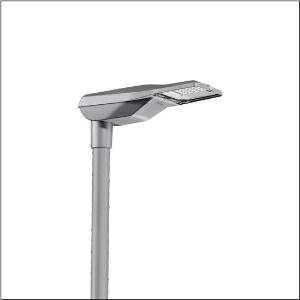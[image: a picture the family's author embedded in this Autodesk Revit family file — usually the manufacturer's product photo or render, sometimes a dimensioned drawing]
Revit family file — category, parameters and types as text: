
# Revit family: streetlight_sl_21_iq_micro___st1_0ab_5xe1m31g08cb_01f6
name_source: partatom
category: Lighting Fixtures
units: mm (PartAtom-declared; Revit-internal decimal feet)

## family parameters
Cut with Voids When Loaded = No
Host = Face
Light Source = No
Part Type = Normal
Room Calculation Point = No
Round Connector Dimension = Use Diameter
Shared = No

## types (1)
- --- (1 x LED, 2520 lm, 19.4 W, 3000K)
    Apparent Load = 19 VA
    CIE Flux Codes = 38 73 97 100 100
    Color Rendering = 70
    Color Temperature = 3000K
    Default Elevation = 1800 mm
    Description = Streetlight SL 21 iQ micro, mast luminaire, primary light control with lens, of PMMA, primary optical cover: cover, of toughened safety glass, transparent, light distribution: ST1.0aB, light emission: direct distribution, primary light characteristic: asymmetric, installation type: post-top, side-entry, LED, High Power LED, rated luminous flux: 2.520lm, luminous efficacy: 130lm/W, light colour: 730, colour temperature: 3000K, control: Street-Remote, Auto-Match, Temp-Guard, Lumen-Switch, Night-Set, Smart-Wire, Light-Fading, Desk-Remote (wireless, voltage-free reading and setting of iQ features in the workshop via application-optimized NFC function/RFID function), optimised constant luminous flux control (CLO 2.0), pre-setting: linear dimming characteristic, mains connection: 220..240V, AC, 50/60Hz, start of lifetime: 19W, end of service life: 20W, reduction: 10W, luminaire housing, of diecast aluminium, powder-coated, Siteco® metallic grey (DB 702S), corrosivity category C5 mid according to DIN EN ISO 12944, please order mast flange separately, inclination adjustable: 0°, 5°, 10°, 15°, sealing non-destructively replaceable, multi-level sealing system, length: 528mm, width: 235mm, height: 110mm, mast flange for spigot size: 42mm (side-entry): 5XC10008XM4, 60/48mm (side-entry/post-top): 5XC10108XM2, 76/60mm (side-entry/post-top): 5XC10108XM1, protection rating (complete): IP66, insulation class (complete): insulation class II (safety insulation), certification: CE, ENEC, ENEC+, VDE, impact resistance: IK09, permissible operating ambient temperature for outdoor applications: -40..+50°C, standard-compliant lighting for roads and squares, packaging unit: 1 piece

Light Distribution: ST1.0aB
    Height = 110 mm
    Lamp = 1 x LED
    Lamp Light Flux = 2520 lm
    Lamp Power = 19.4 W
    Lamp count = 1
    Length = 528 mm
    Luminous efficacy = 130 lm/W
    Manufacturer = Siteco
    ModVariant = No
    Model = 5XE1M31G08CB
    Number of Poles = 1
    OnlyDefault = Yes
    Power Factor = 1
    Product Name = Streetlight SL 21 iQ micro | ST1.0aB
    Product group = mast luminaire | pylon top
    ProductGroupID = 6100
    Protection Class = Protection class II
    Protection Degree = IP 66
    RLX_Detail_Level = 1
    RLX_Emergency_Light_Flux = 0 lm
    RLX_Emergency_Type = 0
    RLX_Emergency_Type_DB = No
    RlxData = <blob elided: 99149 chars, md5=1984a4cd>
    Socket = socket
    Standby Power = 0 W
    System Light Flux = 2520 lm
    System Power = 19 W
    Type Comments = factory setting: luminous flux: 100 % | dim-lin: 254 | 387 mA
    Type Image = l_1006881.jpg
    URL = http://relux.com
    VarID = @adj_107947
    Voltage = 0 V
    Weight = 0.00 kg
    Width = 235 mm

## geometry (parser evidence)
native form markers: Blend x4, Sweep x11
no freeform markers — native parametric forms only
